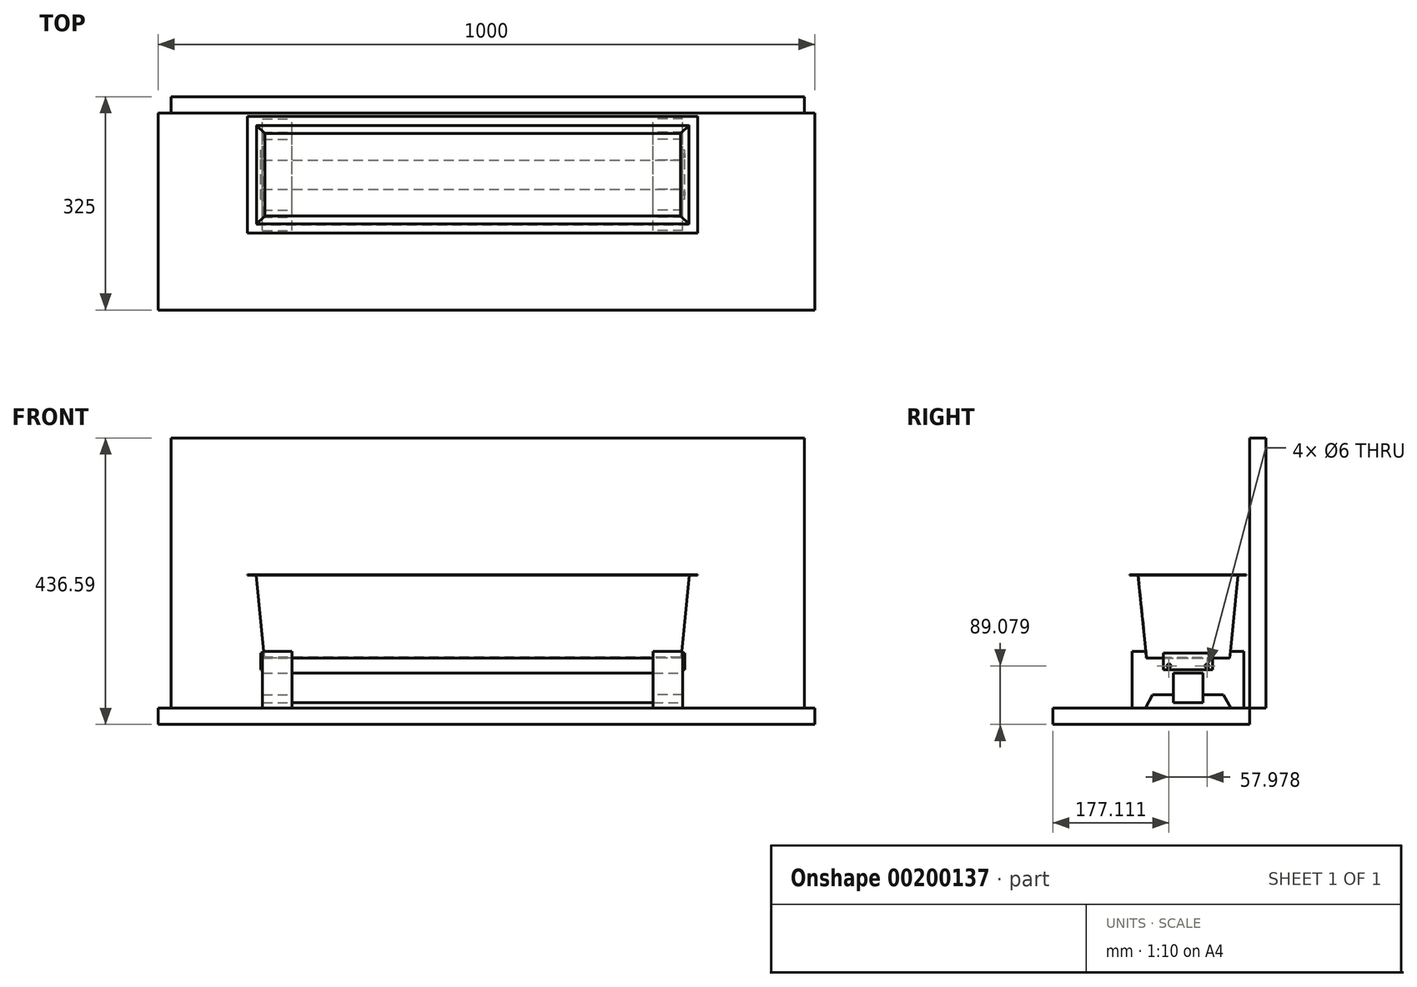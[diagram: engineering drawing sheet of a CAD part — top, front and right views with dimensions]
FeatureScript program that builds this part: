
annotation { "Feature Type Name" : "Feature", "Feature Type Description" : "" }
export const myFeature = defineFeature(function(context is Context, id is Id, definition is map)
    precondition{}
    {
        {
            var Q0;
            Q0=qCreatedBy(makeId("Top.planeOp"),FACE);
            var sketch = newSketch(context, id + "F0", { "sketchPlane" : qUnion([Q0])});
            skLineSegment(sketch, "E0.bottom", {"start": v(317.5, -63.5) * mm, "end": v(-317.5, -63.5) * mm});
            skLineSegment(sketch, "E0.top", {"start": v(317.5, 63.5) * mm, "end": v(-317.5, 63.5) * mm});
            skLineSegment(sketch, "E0.left", {"start": v(317.5, -63.5) * mm, "end": v(317.5, 63.5) * mm});
            skLineSegment(sketch, "E0.right", {"start": v(-317.5, -63.5) * mm, "end": v(-317.5, 63.5) * mm});
            skPoint(sketch, "E0.middle", {"position": v(0, 0) * mm});
            skSolve(sketch);
        }
        {
            var Q0;
            Q0=qCreatedBy(makeId("Top.planeOp"),FACE);
            cPlane(context, id + "F1", {"entities" : qUnion([Q0]), "cplaneType" : CPlaneType.OFFSET, "offset" : (5 * 25.4) * mm, "width" : 150 * mm, "height" : 150 * mm});
        }
        {
            var Q0;
            Q0=qCreatedBy(id+"F1.planeOp",FACE);
            var sketch = newSketch(context, id + "F2", { "sketchPlane" : qUnion([Q0])});
            skLineSegment(sketch, "E1.bottom", {"start": v(330.2, -76.2) * mm, "end": v(-330.2, -76.2) * mm});
            skLineSegment(sketch, "E1.top", {"start": v(330.2, 76.2) * mm, "end": v(-330.2, 76.2) * mm});
            skLineSegment(sketch, "E1.left", {"start": v(330.2, -76.2) * mm, "end": v(330.2, 76.2) * mm});
            skLineSegment(sketch, "E1.right", {"start": v(-330.2, -76.2) * mm, "end": v(-330.2, 76.2) * mm});
            skPoint(sketch, "E1.middle", {"position": v(0, 0) * mm});
            skSolve(sketch);
        }
        {
            var Q0;
            Q0=makeQuery(id+"F0.imprint","IMPRINT",FACE,{"disambiguationData":[TD([[makeQuery(id+"F0.imprint","IMPRINT",EDGE,{"derivedFrom":sQuery(id+"F0.wireOp",EDGE,"E0.bottom")}),-1.0]])]});
            var Q1;
            Q1=makeQuery(id+"F2.imprint","IMPRINT",FACE,{"disambiguationData":[TD([[makeQuery(id+"F2.imprint","IMPRINT",EDGE,{"derivedFrom":sQuery(id+"F2.wireOp",EDGE,"E1.bottom")}),-1.0]])]});
            loft(context, id + "F3", {"sheetProfilesArray" : [{ "sheetProfileEntities" : qUnion([Q0]) }, { "sheetProfileEntities" : qUnion([Q1]) }]});
        }
        {
            var Q0;
            Q0=makeQuery(id+"F3.opLoft","CAP_FACE",FACE,{"disambiguationData":[OSD([makeQuery(id+"F2.imprint","IMPRINT",FACE,{"disambiguationData":[TD([[makeQuery(id+"F2.imprint","IMPRINT",EDGE,{"derivedFrom":sQuery(id+"F2.wireOp",EDGE,"E1.bottom")}),-1.0]])]})])],"isStart":true});
            shell(context, id + "F4", {"entities" : qUnion([Q0]), "thickness" : 1 * mm});
        }
        {
            var Q0;
            Q0=qCreatedBy(id+"F1.planeOp",FACE);
            var sketch = newSketch(context, id + "F5", { "sketchPlane" : qUnion([Q0])});
            skLineSegment(sketch, "E2.bottom", {"start": v(342.9, -88.9) * mm, "end": v(-342.9, -88.9) * mm});
            skLineSegment(sketch, "E2.top", {"start": v(342.9, 88.9) * mm, "end": v(-342.9, 88.9) * mm});
            skLineSegment(sketch, "E2.left", {"start": v(342.9, -88.9) * mm, "end": v(342.9, 88.9) * mm});
            skLineSegment(sketch, "E2.right", {"start": v(-342.9, -88.9) * mm, "end": v(-342.9, 88.9) * mm});
            skPoint(sketch, "E2.middle", {"position": v(0, 0) * mm});
            skLineSegment(sketch, "E3.0", {"start": v(329.2, 75.2) * mm, "end": v(-329.2, 75.2) * mm});
            skLineSegment(sketch, "E4.0", {"start": v(-329.2, 75.2) * mm, "end": v(-329.2, -75.2) * mm});
            skLineSegment(sketch, "E5.0", {"start": v(-329.2, -75.2) * mm, "end": v(329.2, -75.2) * mm});
            skLineSegment(sketch, "E6.0", {"start": v(329.2, -75.2) * mm, "end": v(329.2, 75.2) * mm});
            skSolve(sketch);
        }
        {
            var Q0;
            Q0 = qSketchRegion(id + "F5", true);
            extrude(context, id + "F6", {"entities" : qUnion([Q0]), "operationType" : NewBodyOperationType.ADD, "oppositeDirection" : true, "depth" : 1 * mm});
        }
        {
            var Q0;
            Q0=qCreatedBy(makeId("Top.planeOp"),FACE);
            cPlane(context, id + "F7", {"entities" : qUnion([Q0]), "cplaneType" : CPlaneType.OFFSET, "offset" : (3 * 25.4) * mm, "oppositeDirection" : true, "width" : 150 * mm, "height" : 150 * mm});
        }
        {
            var Q0;
            Q0=qCreatedBy(id+"F7.planeOp",FACE);
            var sketch = newSketch(context, id + "F8", { "sketchPlane" : qUnion([Q0])});
            skLineSegment(sketch, "E7.bottom", {"start": v(-478.97, 93.9) * mm, "end": v(521.03, 93.9) * mm});
            skLineSegment(sketch, "E7.top", {"start": v(-478.97, -206.1) * mm, "end": v(521.03, -206.1) * mm});
            skLineSegment(sketch, "E7.left", {"start": v(-478.97, 93.9) * mm, "end": v(-478.97, -206.1) * mm});
            skLineSegment(sketch, "E7.right", {"start": v(521.03, 93.9) * mm, "end": v(521.03, -206.1) * mm});
            skSolve(sketch);
        }
        {
            var Q0;
            Q0 = qSketchRegion(id + "F8", true);
            extrude(context, id + "F9", {"entities" : qUnion([Q0]), "oppositeDirection" : true, "depth" : 25 * mm});
        }
        {
            var Q0;
            Q0=makeQuery(id+"F9.opExtrude","SWEPT_FACE",FACE,{"disambiguationData":[OSD([sQuery(id+"F8.wireOp",EDGE,"E7.bottom")])]});
            var sketch = newSketch(context, id + "F10", { "sketchPlane" : qUnion([Q0])});
            skLineSegment(sketch, "E8.bottom", {"start": v(-505.42, -76.2) * mm, "end": v(459.2, -76.2) * mm});
            skLineSegment(sketch, "E8.top", {"start": v(-505.42, 335.4) * mm, "end": v(459.2, 335.4) * mm});
            skLineSegment(sketch, "E8.left", {"start": v(-505.42, -76.2) * mm, "end": v(-505.42, 335.4) * mm});
            skLineSegment(sketch, "E8.right", {"start": v(459.2, -76.2) * mm, "end": v(459.2, 335.4) * mm});
            skSolve(sketch);
        }
        {
            var Q0;
            Q0 = qSketchRegion(id + "F10", true);
            extrude(context, id + "F11", {"entities" : qUnion([Q0]), "depth" : 25 * mm});
        }
        {
            var Q0;
            Q0=qCreatedBy(makeId("Right.planeOp"),FACE);
            cPlane(context, id + "F12", {"entities" : qUnion([Q0]), "cplaneType" : CPlaneType.OFFSET, "offset" : 275 * mm, "width" : 150 * mm, "height" : 150 * mm});
        }
        {
            var Q0;
            Q0=qCreatedBy(id+"F12.planeOp",FACE);
            var sketch = newSketch(context, id + "F13", { "sketchPlane" : qUnion([Q0])});
            skLineSegment(sketch, "E9", {"start": v(-85, 10) * mm, "end": v(-64.5, 10) * mm});
            skLineSegment(sketch, "E10", {"start": v(-64.5, 10) * mm, "end": v(-63.5, 0) * mm});
            skLineSegment(sketch, "E11", {"start": v(-63.5, 0) * mm, "end": v(63.5, 0) * mm});
            skLineSegment(sketch, "E12", {"start": v(63.5, 0) * mm, "end": v(64.5, 10) * mm});
            skLineSegment(sketch, "E13", {"start": v(64.5, 10) * mm, "end": v(85, 10) * mm});
            skLineSegment(sketch, "E14", {"start": v(85, 10) * mm, "end": v(85, -76.2) * mm});
            skLineSegment(sketch, "E15", {"start": v(-85, -76.2) * mm, "end": v(-85, 10) * mm});
            skLineSegment(sketch, "E16", {"start": v(-85, -76.2) * mm, "end": v(-65, -76.2) * mm});
            skLineSegment(sketch, "E17", {"start": v(-65, -76.2) * mm, "end": v(-53.89, -56.2) * mm});
            skLineSegment(sketch, "E18", {"start": v(-53.89, -56.2) * mm, "end": v(-22.5, -56.2) * mm});
            skLineSegment(sketch, "E19", {"start": v(53.89, -56.2) * mm, "end": v(65, -76.2) * mm});
            skLineSegment(sketch, "E20", {"start": v(65, -76.2) * mm, "end": v(85, -76.2) * mm});
            skLineSegment(sketch, "E21", {"start": v(0, 77.48) * mm, "end": v(0, -96.3) * mm, "construction": true});
            skLineSegment(sketch, "E22.bottom", {"start": v(-22.5, -23.1) * mm, "end": v(22.5, -23.1) * mm});
            skLineSegment(sketch, "E22.left", {"start": v(-22.5, -23.1) * mm, "end": v(-22.5, -56.2) * mm});
            skLineSegment(sketch, "E22.right", {"start": v(22.5, -23.1) * mm, "end": v(22.5, -56.2) * mm});
            skLineSegment(sketch, "E23.trimOffspring", {"start": v(22.5, -56.2) * mm, "end": v(53.89, -56.2) * mm});
            skSolve(sketch);
        }
        {
            var Q0;
            Q0 = qSketchRegion(id + "F13", true);
            extrude(context, id + "F14", {"entities" : qUnion([Q0]), "depth" : 45 * mm});
        }
        {
            var Q0;
            Q0=makeQuery(id+"F14.opExtrude","CAP_FACE",FACE,{"disambiguationData":[OSD([sQuery(id+"F13.wireOp",EDGE,"E9"),sQuery(id+"F13.wireOp",EDGE,"E10"),sQuery(id+"F13.wireOp",EDGE,"E11"),sQuery(id+"F13.wireOp",EDGE,"E12"),sQuery(id+"F13.wireOp",EDGE,"E13"),sQuery(id+"F13.wireOp",EDGE,"E14"),sQuery(id+"F13.wireOp",EDGE,"E15"),sQuery(id+"F13.wireOp",EDGE,"E16"),sQuery(id+"F13.wireOp",EDGE,"E17"),sQuery(id+"F13.wireOp",EDGE,"E18"),sQuery(id+"F13.wireOp",EDGE,"E19"),sQuery(id+"F13.wireOp",EDGE,"E20"),sQuery(id+"F13.wireOp",EDGE,"E22.bottom"),sQuery(id+"F13.wireOp",EDGE,"E22.left"),sQuery(id+"F13.wireOp",EDGE,"E22.right"),sQuery(id+"F13.wireOp",EDGE,"E23.trimOffspring")])],"isStart":false});
            var sketch = newSketch(context, id + "F15", { "sketchPlane" : qUnion([Q0])});
            skLineSegment(sketch, "E24.bottom", {"start": v(-37.5, 7.38) * mm, "end": v(37.5, 7.38) * mm});
            skLineSegment(sketch, "E24.top", {"start": v(-37.5, -17.62) * mm, "end": v(37.5, -17.62) * mm});
            skLineSegment(sketch, "E24.left", {"start": v(-37.5, 7.38) * mm, "end": v(-37.5, -17.62) * mm});
            skLineSegment(sketch, "E24.right", {"start": v(37.5, 7.38) * mm, "end": v(37.5, -17.62) * mm});
            skLineSegment(sketch, "E25", {"start": v(-101.2, -5.12) * mm, "end": v(152.24, -5.12) * mm, "construction": true});
            skPoint(sketch, "E25.startSnap0", {"position": v(-37.5, -5.12) * mm});
            skLineSegment(sketch, "E26", {"start": v(0, 40.9) * mm, "end": v(0, -54.84) * mm, "construction": true});
            skPoint(sketch, "E26.endSnap0", {"position": v(0, -23.1) * mm});
            skCircle(sketch, "E27", {"center": v(-28.99, -12.12) * mm, "radius": 3 * mm});
            skCircle(sketch, "E28", {"center": v(28.99, -12.12) * mm, "radius": 3 * mm});
            skSolve(sketch);
        }
        {
            var Q0;
            Q0 = qSketchRegion(id + "F15", true);
            extrude(context, id + "F16", {"entities" : qUnion([Q0]), "depth" : 3 * mm});
        }
        {
            var Q0;
            Q0=makeQuery(id+"F14.opExtrude","SWEPT_BODY",BODY,{"disambiguationData":[OSD([sQuery(id+"F13.wireOp",EDGE,"E9"),sQuery(id+"F13.wireOp",EDGE,"E10"),sQuery(id+"F13.wireOp",EDGE,"E11"),sQuery(id+"F13.wireOp",EDGE,"E12"),sQuery(id+"F13.wireOp",EDGE,"E13"),sQuery(id+"F13.wireOp",EDGE,"E14"),sQuery(id+"F13.wireOp",EDGE,"E15"),sQuery(id+"F13.wireOp",EDGE,"E16"),sQuery(id+"F13.wireOp",EDGE,"E17"),sQuery(id+"F13.wireOp",EDGE,"E18"),sQuery(id+"F13.wireOp",EDGE,"E19"),sQuery(id+"F13.wireOp",EDGE,"E20"),sQuery(id+"F13.wireOp",EDGE,"E22.bottom"),sQuery(id+"F13.wireOp",EDGE,"E22.left"),sQuery(id+"F13.wireOp",EDGE,"E22.right"),sQuery(id+"F13.wireOp",EDGE,"E23.trimOffspring")])]});
            var Q1;
            Q1=makeQuery(id+"F16.opExtrude","SWEPT_BODY",BODY,{"disambiguationData":[OSD([sQuery(id+"F15.wireOp",EDGE,"E24.bottom"),sQuery(id+"F15.wireOp",EDGE,"E24.top"),sQuery(id+"F15.wireOp",EDGE,"E24.left"),sQuery(id+"F15.wireOp",EDGE,"E24.right"),sQuery(id+"F15.wireOp",EDGE,"E27"),sQuery(id+"F15.wireOp",EDGE,"E28")])]});
            var Q2;
            Q2=qCreatedBy(makeId("Right.planeOp"),FACE);
            mirror(context, id + "F17", {"entities" : qUnion([Q0, Q1]), "mirrorPlane" : qUnion([Q2])});
        }
        {
            var Q0;
            Q0=makeQuery(id+"F14.opExtrude","CAP_FACE",FACE,{"disambiguationData":[OSD([sQuery(id+"F13.wireOp",EDGE,"E9"),sQuery(id+"F13.wireOp",EDGE,"E10"),sQuery(id+"F13.wireOp",EDGE,"E11"),sQuery(id+"F13.wireOp",EDGE,"E12"),sQuery(id+"F13.wireOp",EDGE,"E13"),sQuery(id+"F13.wireOp",EDGE,"E14"),sQuery(id+"F13.wireOp",EDGE,"E15"),sQuery(id+"F13.wireOp",EDGE,"E16"),sQuery(id+"F13.wireOp",EDGE,"E17"),sQuery(id+"F13.wireOp",EDGE,"E18"),sQuery(id+"F13.wireOp",EDGE,"E19"),sQuery(id+"F13.wireOp",EDGE,"E20"),sQuery(id+"F13.wireOp",EDGE,"E22.bottom"),sQuery(id+"F13.wireOp",EDGE,"E22.left"),sQuery(id+"F13.wireOp",EDGE,"E22.right"),sQuery(id+"F13.wireOp",EDGE,"E23.trimOffspring")])],"isStart":false});
            var sketch = newSketch(context, id + "F18", { "sketchPlane" : qUnion([Q0])});
            skLineSegment(sketch, "E29.bottom", {"start": v(-22.5, -23.1) * mm, "end": v(22.5, -23.1) * mm});
            skLineSegment(sketch, "E29.top", {"start": v(-22.5, -68.1) * mm, "end": v(22.5, -68.1) * mm});
            skLineSegment(sketch, "E29.left", {"start": v(-22.5, -23.1) * mm, "end": v(-22.5, -68.1) * mm});
            skLineSegment(sketch, "E29.right", {"start": v(22.5, -23.1) * mm, "end": v(22.5, -68.1) * mm});
            skSolve(sketch);
        }
        {
            var Q0;
            Q0 = qSketchRegion(id + "F18", true);
            var Q1;
            Q1=makeQuery(id+"F17.opPattern","COPY",FACE,{"derivedFrom":makeQuery(id+"F14.opExtrude","CAP_FACE",FACE,{"disambiguationData":[OSD([sQuery(id+"F13.wireOp",EDGE,"E9"),sQuery(id+"F13.wireOp",EDGE,"E10"),sQuery(id+"F13.wireOp",EDGE,"E11"),sQuery(id+"F13.wireOp",EDGE,"E12"),sQuery(id+"F13.wireOp",EDGE,"E13"),sQuery(id+"F13.wireOp",EDGE,"E14"),sQuery(id+"F13.wireOp",EDGE,"E15"),sQuery(id+"F13.wireOp",EDGE,"E16"),sQuery(id+"F13.wireOp",EDGE,"E17"),sQuery(id+"F13.wireOp",EDGE,"E18"),sQuery(id+"F13.wireOp",EDGE,"E19"),sQuery(id+"F13.wireOp",EDGE,"E20"),sQuery(id+"F13.wireOp",EDGE,"E22.bottom"),sQuery(id+"F13.wireOp",EDGE,"E22.left"),sQuery(id+"F13.wireOp",EDGE,"E22.right"),sQuery(id+"F13.wireOp",EDGE,"E23.trimOffspring")])],"isStart":false}),"instanceName":"1"});
            extrude(context, id + "F19", {"entities" : qUnion([Q0]), "endBound" : BoundingType.UP_TO_SURFACE, "oppositeDirection" : true, "endBoundEntityFace" : qUnion([Q1]), "depth" : 25 * mm});
        }
    });
